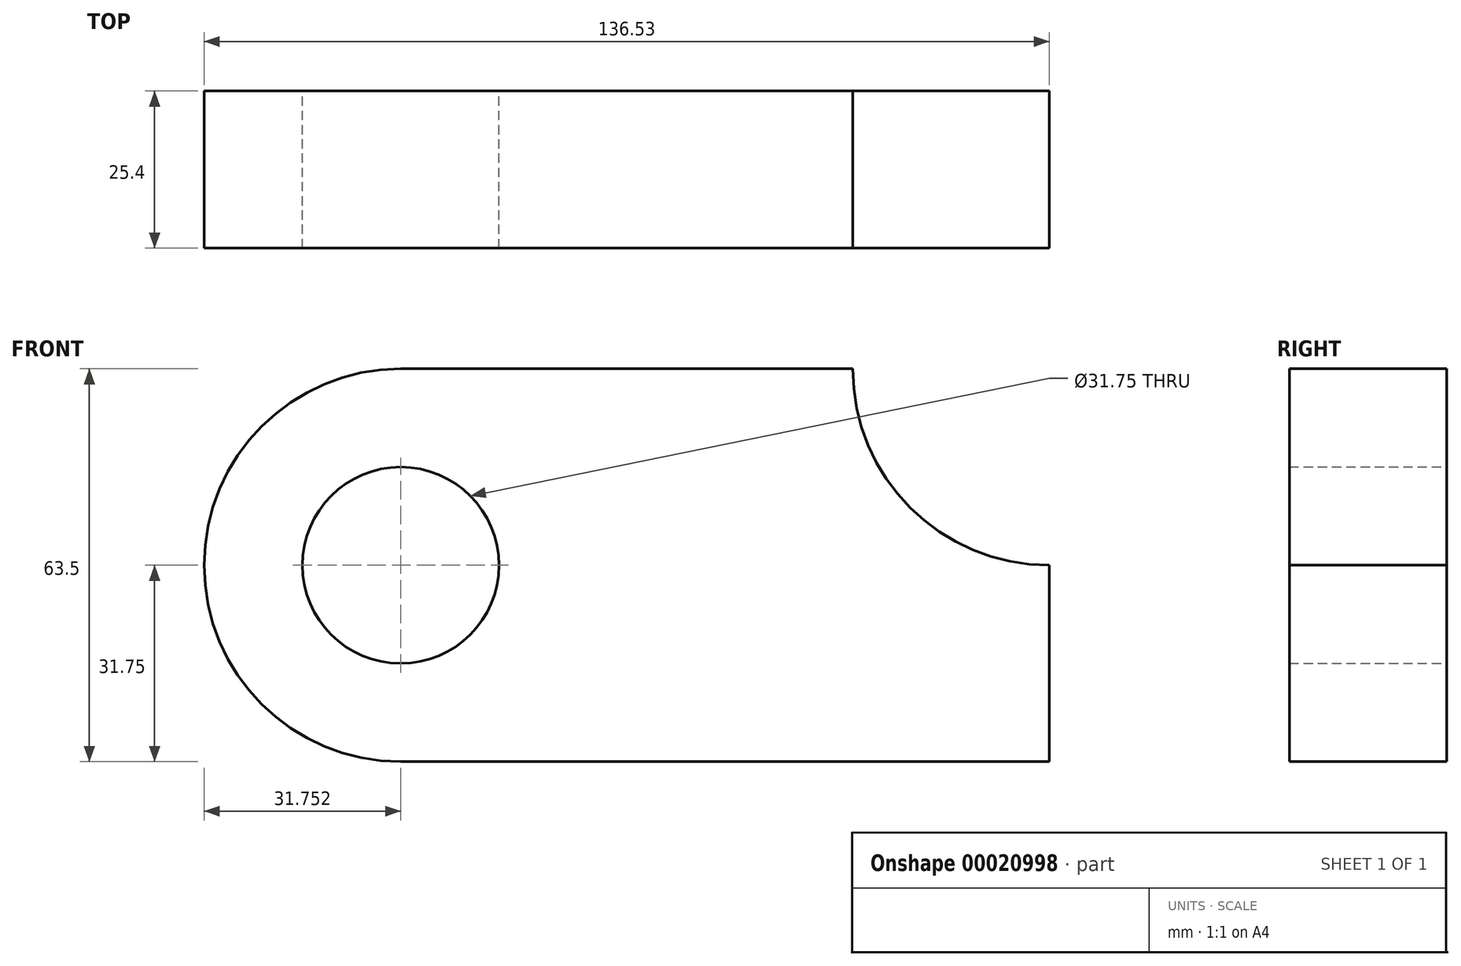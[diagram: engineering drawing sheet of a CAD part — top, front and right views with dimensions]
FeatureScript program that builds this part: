
annotation { "Feature Type Name" : "Feature", "Feature Type Description" : "" }
export const myFeature = defineFeature(function(context is Context, id is Id, definition is map)
    precondition{}
    {
        {
            var Q0;
            Q0=qCreatedBy(makeId("Front.planeOp"),FACE);
            var sketch = newSketch(context, id + "F0", { "sketchPlane" : qUnion([Q0])});
            skLineSegment(sketch, "E0.rect.bottom", {"start": v(-52.39, 31.75) * mm, "end": v(20.64, 31.75) * mm});
            skLineSegment(sketch, "E0.rect.top", {"start": v(-52.39, -31.75) * mm, "end": v(52.39, -31.75) * mm});
            skLineSegment(sketch, "E0.rect.right", {"start": v(52.39, 0) * mm, "end": v(52.39, -31.75) * mm});
            skPoint(sketch, "E0.rect.middle", {"position": v(0, 0) * mm});
            skArc(sketch, "E1", {"start": v(-52.39, 31.75) * mm, "mid": v(-84.14, 0) * mm, "end": v(-52.39, -31.75) * mm});
            skCircle(sketch, "E2", {"center": v(-52.39, 0) * mm, "radius": 15.88 * mm});
            skPoint(sketch, "E3.center.orphan", {"position": v(52.39, 0) * mm});
            skArc(sketch, "E4", {"start": v(20.64, 31.75) * mm, "mid": v(29.94, 9.3) * mm, "end": v(52.39, 0) * mm});
            skSolve(sketch);
        }
        {
            var Q0;
            Q0 = qSketchRegion(id + "F0", true);
            extrude(context, id + "F1", {"entities" : qUnion([Q0]), "depth" : 25.4 * mm});
        }
    });
